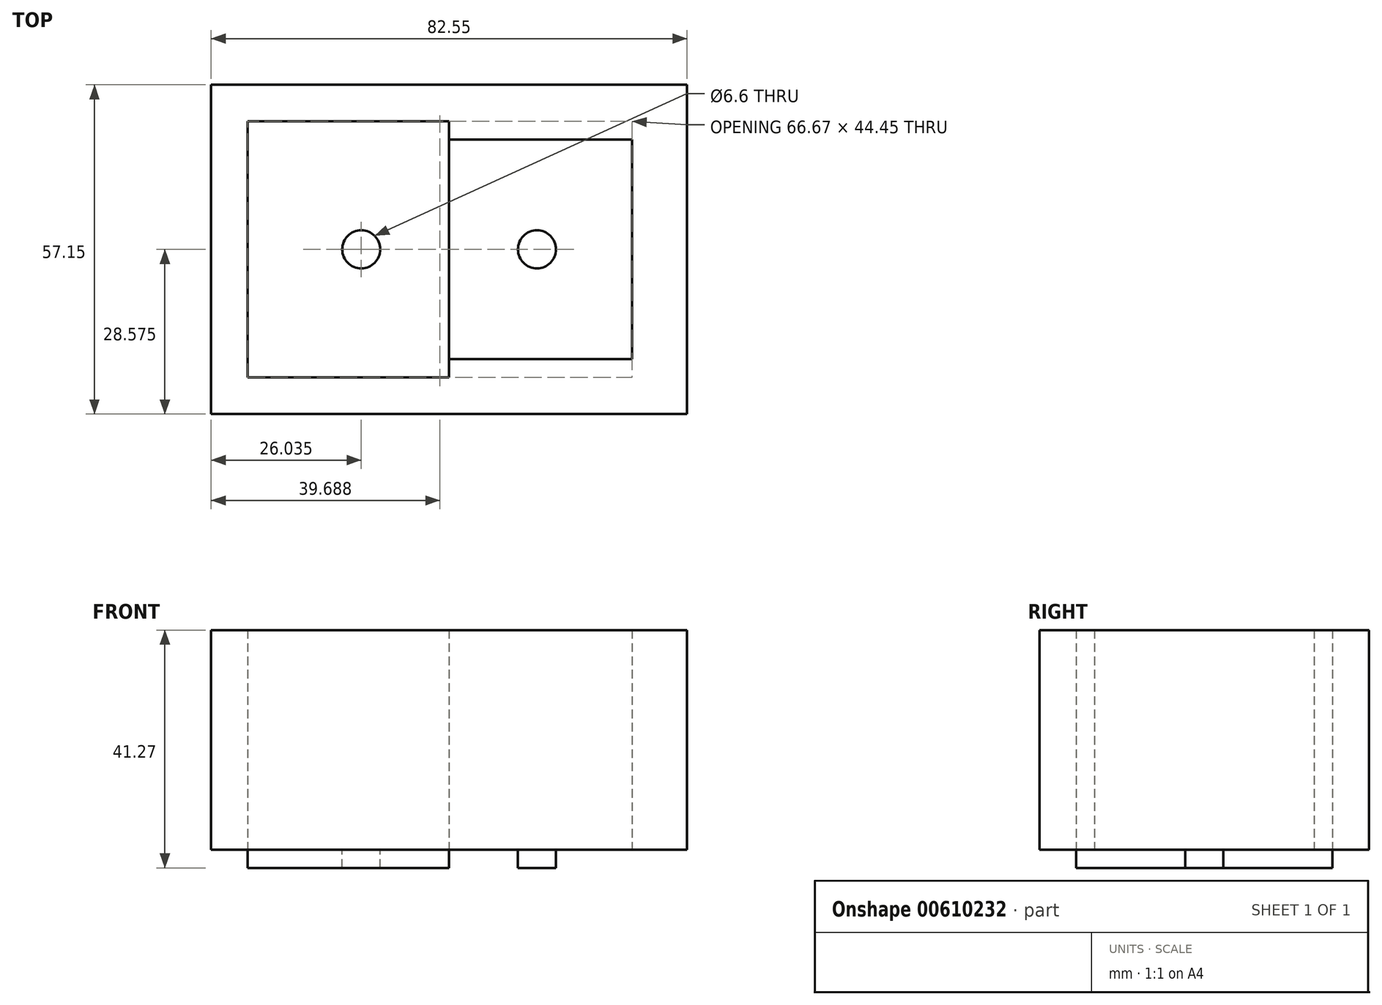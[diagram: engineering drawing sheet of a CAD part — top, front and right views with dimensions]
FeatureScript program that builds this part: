
annotation { "Feature Type Name" : "Feature", "Feature Type Description" : "" }
export const myFeature = defineFeature(function(context is Context, id is Id, definition is map)
    precondition{}
    {
        {
            var Q0;
            Q0=qCreatedBy(makeId("Top.planeOp"),FACE);
            var sketch = newSketch(context, id + "F0", { "sketchPlane" : qUnion([Q0])});
            skLineSegment(sketch, "E0.bottom", {"start": v(0, 0) * mm, "end": v(69.85, 0) * mm});
            skLineSegment(sketch, "E0.top", {"start": v(0, -44.45) * mm, "end": v(69.85, -44.45) * mm});
            skLineSegment(sketch, "E0.left", {"start": v(0, 0) * mm, "end": v(0, -44.45) * mm});
            skLineSegment(sketch, "E0.right", {"start": v(69.85, 0) * mm, "end": v(69.85, -44.45) * mm});
            skSolve(sketch);
        }
        {
            var Q0;
            Q0=makeQuery(id+"F0.imprint","IMPRINT",FACE,{"disambiguationData":[TD([[makeQuery(id+"F0.imprint","IMPRINT",EDGE,{"derivedFrom":sQuery(id+"F0.wireOp",EDGE,"E0.bottom")}),-1.0]])]});
            extrude(context, id + "F1", {"entities" : qUnion([Q0]), "depth" : 3.17 * mm, "offsetDistance" : 25.4 * mm});
        }
        {
            var Q0;
            Q0=makeQuery(id+"F1.opExtrude","CAP_FACE",FACE,{"disambiguationData":[OSD([sQuery(id+"F0.wireOp",EDGE,"E0.bottom"),sQuery(id+"F0.wireOp",EDGE,"E0.top"),sQuery(id+"F0.wireOp",EDGE,"E0.left"),sQuery(id+"F0.wireOp",EDGE,"E0.right")])],"isStart":false});
            var sketch = newSketch(context, id + "F2", { "sketchPlane" : qUnion([Q0])});
            skLineSegment(sketch, "E1", {"start": v(34.93, 0) * mm, "end": v(34.93, -44.45) * mm});
            skLineSegment(sketch, "E2", {"start": v(0, -22.23) * mm, "end": v(69.85, -22.23) * mm});
            skCircle(sketch, "E3", {"center": v(19.69, -22.23) * mm, "radius": 3.3 * mm});
            skCircle(sketch, "E4.MirrorC", {"center": v(50.16, -22.23) * mm, "radius": 3.3 * mm});
            skSolve(sketch);
        }
        {
            var Q0;
            {var subQ0=sQuery(id+"F2.wireOp",EDGE,"E3");var subQ1=sQuery(id+"F2.wireOp",EDGE,"E2");var subQ2=makeQuery(id+"F2.imprint","INTERSECT",VERTEX,{"disambiguationData":[OD(0.0)],"derivedFrom":[subQ1,subQ0]});Q0=makeQuery(id+"F2.imprint","IMPRINT",FACE,{"disambiguationData":[TD([[makeQuery(id+"F2.imprint","IMPRINT",EDGE,{"disambiguationData":[TD([[subQ2,-1.0]])],"derivedFrom":subQ1}),-1.0]])]});}
            var Q1;
            {var subQ0=sQuery(id+"F2.wireOp",EDGE,"E3");var subQ1=sQuery(id+"F2.wireOp",EDGE,"E2");var subQ2=makeQuery(id+"F2.imprint","INTERSECT",VERTEX,{"disambiguationData":[OD(0.0)],"derivedFrom":[subQ1,subQ0]});Q1=makeQuery(id+"F2.imprint","IMPRINT",FACE,{"disambiguationData":[TD([[makeQuery(id+"F2.imprint","IMPRINT",EDGE,{"disambiguationData":[TD([[subQ2,-1.0]])],"derivedFrom":subQ1}),1.0]])]});}
            var Q2;
            {var subQ0=sQuery(id+"F2.wireOp",EDGE,"E4.MirrorC");var subQ1=sQuery(id+"F2.wireOp",EDGE,"E2");var subQ2=makeQuery(id+"F2.imprint","INTERSECT",VERTEX,{"disambiguationData":[OD(0.0)],"derivedFrom":[subQ1,subQ0]});Q2=makeQuery(id+"F2.imprint","IMPRINT",FACE,{"disambiguationData":[TD([[makeQuery(id+"F2.imprint","IMPRINT",EDGE,{"disambiguationData":[TD([[subQ2,-1.0]])],"derivedFrom":subQ1}),1.0]])]});}
            var Q3;
            {var subQ0=sQuery(id+"F2.wireOp",EDGE,"E4.MirrorC");var subQ1=sQuery(id+"F2.wireOp",EDGE,"E2");var subQ2=makeQuery(id+"F2.imprint","INTERSECT",VERTEX,{"disambiguationData":[OD(0.0)],"derivedFrom":[subQ1,subQ0]});Q3=makeQuery(id+"F2.imprint","IMPRINT",FACE,{"disambiguationData":[TD([[makeQuery(id+"F2.imprint","IMPRINT",EDGE,{"disambiguationData":[TD([[subQ2,-1.0]])],"derivedFrom":subQ1}),-1.0]])]});}
            extrude(context, id + "F3", {"entities" : qUnion([Q0, Q1, Q2, Q3]), "operationType" : NewBodyOperationType.REMOVE, "endBound" : BoundingType.UP_TO_NEXT, "oppositeDirection" : true, "depth" : 25.4 * mm, "offsetDistance" : 25.4 * mm});
        }
        {
            var Q0;
            Q0=makeQuery(id+"F1.opExtrude","CAP_FACE",FACE,{"disambiguationData":[OSD([sQuery(id+"F0.wireOp",EDGE,"E0.bottom"),sQuery(id+"F0.wireOp",EDGE,"E0.top"),sQuery(id+"F0.wireOp",EDGE,"E0.left"),sQuery(id+"F0.wireOp",EDGE,"E0.right")])],"isStart":false});
            var sketch = newSketch(context, id + "F4", { "sketchPlane" : qUnion([Q0])});
            skLineSegment(sketch, "E5.0", {"start": v(66.68, -3.17) * mm, "end": v(66.68, -41.28) * mm});
            skLineSegment(sketch, "E5.1", {"start": v(3.17, -3.17) * mm, "end": v(66.68, -3.17) * mm});
            skLineSegment(sketch, "E5.2", {"start": v(3.17, -3.17) * mm, "end": v(3.17, -41.28) * mm});
            skLineSegment(sketch, "E5.3", {"start": v(3.17, -41.28) * mm, "end": v(66.68, -41.28) * mm});
            skLineSegment(sketch, "E6.0", {"start": v(-6.35, 6.35) * mm, "end": v(-6.35, -50.8) * mm});
            skLineSegment(sketch, "E6.1", {"start": v(76.2, 6.35) * mm, "end": v(-6.35, 6.35) * mm});
            skLineSegment(sketch, "E6.2", {"start": v(76.2, -50.8) * mm, "end": v(76.2, 6.35) * mm});
            skLineSegment(sketch, "E6.3", {"start": v(-6.35, -50.8) * mm, "end": v(76.2, -50.8) * mm});
            skSolve(sketch);
        }
        {
            var Q0;
            Q0=makeQuery(id+"F4.imprint","IMPRINT",FACE,{"disambiguationData":[TD([[makeQuery(id+"F4.imprint","IMPRINT",EDGE,{"derivedFrom":sQuery(id+"F4.wireOp",EDGE,"E5.0")}),1.0]])]});
            extrude(context, id + "F5", {"entities" : qUnion([Q0]), "operationType" : NewBodyOperationType.ADD, "depth" : 38.1 * mm, "offsetDistance" : 25.4 * mm});
        }
    });
